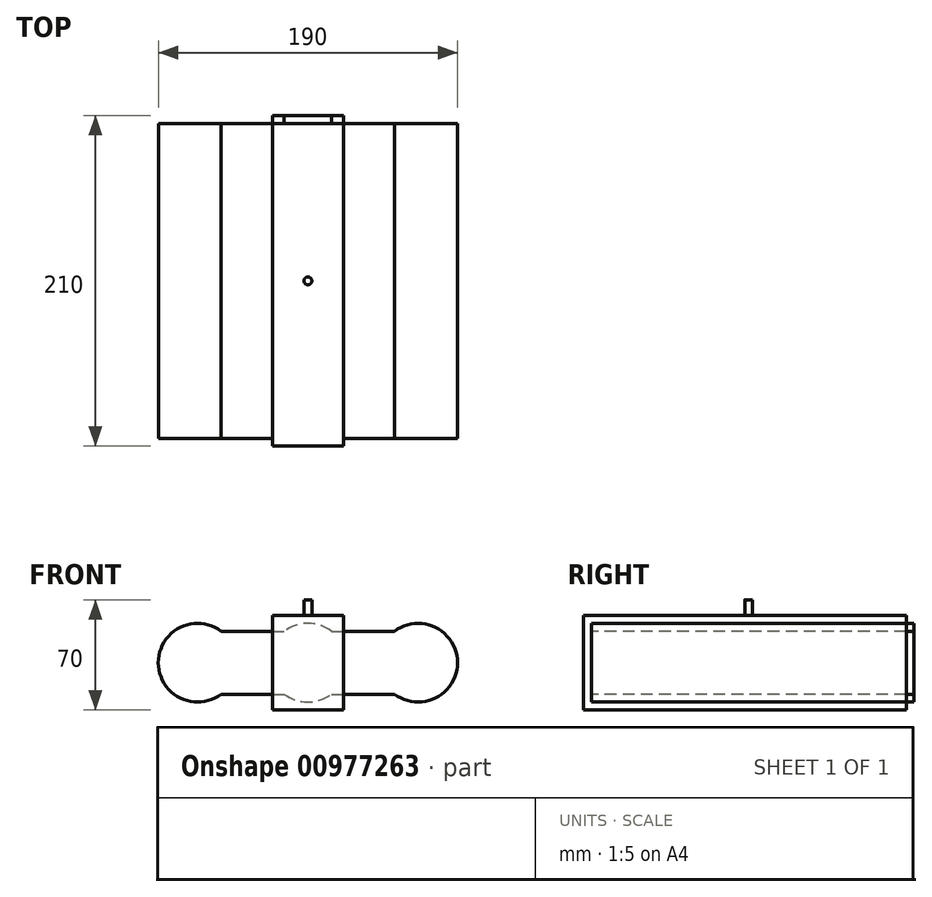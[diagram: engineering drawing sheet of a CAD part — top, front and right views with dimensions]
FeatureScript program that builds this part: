
annotation { "Feature Type Name" : "Feature", "Feature Type Description" : "" }
export const myFeature = defineFeature(function(context is Context, id is Id, definition is map)
    precondition{}
    {
        {
            var Q0;
            Q0=qCreatedBy(makeId("Front.planeOp"),FACE);
            var sketch = newSketch(context, id + "F0", { "sketchPlane" : qUnion([Q0])});
            skCircle(sketch, "E0", {"center": v(70, 0) * mm, "radius": 25 * mm});
            skCircle(sketch, "E1", {"center": v(0, 0) * mm, "radius": 25 * mm});
            skCircle(sketch, "E2", {"center": v(-70, 0) * mm, "radius": 25 * mm});
            skLineSegment(sketch, "E3.bottom", {"start": v(-70, 20) * mm, "end": v(70, 20) * mm});
            skLineSegment(sketch, "E3.top", {"start": v(-70, -20) * mm, "end": v(70, -20) * mm});
            skLineSegment(sketch, "E3.left", {"start": v(-70, 20) * mm, "end": v(-70, -20) * mm});
            skLineSegment(sketch, "E3.right", {"start": v(70, 20) * mm, "end": v(70, -20) * mm});
            skSolve(sketch);
        }
        {
            var Q0;
            Q0=qSketchRegion(id+"F0",true);
            extrude(context, id + "F1", {"entities" : qUnion([Q0]), "depth" : 200 * mm, "offsetDistance" : 25 * mm, "symmetric" : true});
        }
        {
            var Q0;
            Q0=qCreatedBy(makeId("Front.planeOp"),FACE);
            var sketch = newSketch(context, id + "F2", { "sketchPlane" : qUnion([Q0])});
            skCircle(sketch, "E4", {"center": v(70, 0) * mm, "radius": 25 * mm});
            skCircle(sketch, "E5", {"center": v(0, 0) * mm, "radius": 25 * mm});
            skCircle(sketch, "E6", {"center": v(-70, 0) * mm, "radius": 25 * mm});
            skLineSegment(sketch, "E7.bottom", {"start": v(-70, 20) * mm, "end": v(70, 20) * mm});
            skLineSegment(sketch, "E7.top", {"start": v(-70, -20) * mm, "end": v(70, -20) * mm});
            skLineSegment(sketch, "E7.left", {"start": v(-70, 20) * mm, "end": v(-70, -20) * mm});
            skLineSegment(sketch, "E7.right", {"start": v(70, 20) * mm, "end": v(70, -20) * mm});
            skLineSegment(sketch, "E8.bottom", {"start": v(-22.5, 30) * mm, "end": v(22.5, 30) * mm});
            skLineSegment(sketch, "E8.top", {"start": v(-22.5, -30) * mm, "end": v(22.5, -30) * mm});
            skLineSegment(sketch, "E8.left", {"start": v(-22.5, 30) * mm, "end": v(-22.5, -30) * mm});
            skLineSegment(sketch, "E8.right", {"start": v(22.5, 30) * mm, "end": v(22.5, -30) * mm});
            skSolve(sketch);
        }
        {
            var Q0;
            {var subQ8=sQuery(id+"F2.wireOp",EDGE,"E8.bottom");Q0=makeQuery(id+"F2.imprint","IMPRINT",FACE,{"disambiguationData":[TD([[makeQuery(id+"F2.imprint","IMPRINT",EDGE,{"derivedFrom":subQ8}),-1.0]])]});}
            var Q1;
            {var subQ0=sQuery(id+"F2.wireOp",EDGE,"E8.top");Q1=makeQuery(id+"F2.imprint","IMPRINT",FACE,{"disambiguationData":[TD([[makeQuery(id+"F2.imprint","IMPRINT",EDGE,{"derivedFrom":subQ0}),1.0]])]});}
            extrude(context, id + "F3", {"entities" : qUnion([Q0, Q1]), "oppositeDirection" : true, "depth" : 210 * mm, "offsetDistance" : 25 * mm, "symmetric" : true});
        }
        {
            var Q0;
            Q0=makeQuery(id+"F3.opExtrude","CAP_FACE",FACE,{"disambiguationData":[OSD([sQuery(id+"F2.wireOp",EDGE,"E5"),sQuery(id+"F2.wireOp",EDGE,"E7.bottom"),sQuery(id+"F2.wireOp",EDGE,"E8.bottom"),sQuery(id+"F2.wireOp",EDGE,"E8.left"),sQuery(id+"F2.wireOp",EDGE,"E8.right")])],"isStart":true});
            var sketch = newSketch(context, id + "F4", { "sketchPlane" : qUnion([Q0])});
            skLineSegment(sketch, "E9.bottom", {"start": v(-22.5, 30) * mm, "end": v(22.5, 30) * mm});
            skLineSegment(sketch, "E9.top", {"start": v(-22.5, -30) * mm, "end": v(22.5, -30) * mm});
            skLineSegment(sketch, "E9.left", {"start": v(-22.5, 30) * mm, "end": v(-22.5, -30) * mm});
            skLineSegment(sketch, "E9.right", {"start": v(22.5, 30) * mm, "end": v(22.5, -30) * mm});
            skSolve(sketch);
        }
        {
            var Q0;
            {var subQ5=sQuery(id+"F4.wireOp",EDGE,"E9.top");Q0=makeQuery(id+"F4.imprint","IMPRINT",FACE,{"disambiguationData":[TD([[makeQuery(id+"F4.imprint","IMPRINT",EDGE,{"derivedFrom":subQ5}),1.0]])]});}
            extrude(context, id + "F5", {"entities" : qUnion([Q0]), "operationType" : NewBodyOperationType.ADD, "oppositeDirection" : true, "depth" : 5 * mm, "offsetDistance" : 25 * mm});
        }
        {
            var Q0;
            Q0=qSketchRegion(id+"F4",true);
            extrude(context, id + "F6", {"entities" : qUnion([Q0]), "oppositeDirection" : true, "depth" : 210 * mm, "offsetDistance" : 25 * mm, "hasSecondDirection" : true, "secondDirectionOppositeDirection" : true, "secondDirectionDepth" : 205 * mm});
        }
        {
            var Q0;
            Q0=makeQuery(id+"F3.opExtrude","CAP_FACE",FACE,{"disambiguationData":[OSD([sQuery(id+"F2.wireOp",EDGE,"E5"),sQuery(id+"F2.wireOp",EDGE,"E7.bottom"),sQuery(id+"F2.wireOp",EDGE,"E8.bottom"),sQuery(id+"F2.wireOp",EDGE,"E8.left"),sQuery(id+"F2.wireOp",EDGE,"E8.right")])],"isStart":false});
            var Q1;
            Q1=makeQuery(id+"F3.opExtrude","CAP_FACE",FACE,{"disambiguationData":[OSD([sQuery(id+"F2.wireOp",EDGE,"E5"),sQuery(id+"F2.wireOp",EDGE,"E7.top"),sQuery(id+"F2.wireOp",EDGE,"E8.top"),sQuery(id+"F2.wireOp",EDGE,"E8.left"),sQuery(id+"F2.wireOp",EDGE,"E8.right")])],"isStart":false});
            extrude(context, id + "F7", {"entities" : qUnion([Q0, Q1]), "operationType" : NewBodyOperationType.REMOVE, "oppositeDirection" : true, "depth" : 5 * mm, "offsetDistance" : 25 * mm});
        }
        {
            var Q0;
            Q0=makeQuery(id+"F6.opExtrude","CAP_FACE",FACE,{"disambiguationData":[OSD([sQuery(id+"F4.wireOp",EDGE,"E9.bottom"),sQuery(id+"F4.wireOp",EDGE,"E9.top"),sQuery(id+"F4.wireOp",EDGE,"E9.left"),sQuery(id+"F4.wireOp",EDGE,"E9.right")])],"isStart":false});
            var sketch = newSketch(context, id + "F8", { "sketchPlane" : qUnion([Q0])});
            skPoint(sketch, "E10", {"position": v(17.5, 25) * mm});
            skPoint(sketch, "E11", {"position": v(-17.5, -25) * mm});
            skSolve(sketch);
        }
        {
            var Q0;
            Q0=sQuery(id+"F8.wireOp",VERTEX,"E11");
            var Q1;
            Q1=sQuery(id+"F8.wireOp",VERTEX,"E10");
            var Q2;
            Q2=makeQuery(id+"F3.opExtrude","SWEPT_BODY",BODY,{"disambiguationData":[OSD([sQuery(id+"F2.wireOp",EDGE,"E5"),sQuery(id+"F2.wireOp",EDGE,"E7.bottom"),sQuery(id+"F2.wireOp",EDGE,"E8.bottom"),sQuery(id+"F2.wireOp",EDGE,"E8.left"),sQuery(id+"F2.wireOp",EDGE,"E8.right")])]});
            var Q3;
            Q3=makeQuery(id+"F6.opExtrude","SWEPT_BODY",BODY,{"disambiguationData":[OSD([sQuery(id+"F4.wireOp",EDGE,"E9.bottom"),sQuery(id+"F4.wireOp",EDGE,"E9.top"),sQuery(id+"F4.wireOp",EDGE,"E9.left"),sQuery(id+"F4.wireOp",EDGE,"E9.right")])]});
            hole(context, id + "F9", {"style" : HoleStyle.SIMPLE, "endStyle" : HoleEndStyle.BLIND, "holeDiameter" : 5 * mm, "majorDiameter" : 5 * mm, "holeDepth" : 20 * mm, "isTappedThrough" : true, "tappedDepth" : 12 * mm, "tapClearance" : 3, "locations" : qUnion([Q0, Q1]), "scope" : qUnion([Q2, Q3])});
        }
        {
            var Q0;
            Q0=makeQuery(id+"F3.opExtrude","SWEPT_FACE",FACE,{"disambiguationData":[OSD([sQuery(id+"F2.wireOp",EDGE,"E8.bottom")])]});
            var sketch = newSketch(context, id + "F10", { "sketchPlane" : qUnion([Q0])});
            skPoint(sketch, "E12", {"position": v(0, 0) * mm});
            skCircle(sketch, "E13", {"center": v(0, 0) * mm, "radius": 2.5 * mm});
            skSolve(sketch);
        }
        {
            var Q0;
            Q0=qSketchRegion(id+"F10",true);
            extrude(context, id + "F11", {"entities" : qUnion([Q0]), "operationType" : NewBodyOperationType.ADD, "depth" : 10 * mm, "offsetDistance" : 25 * mm});
        }
    });
